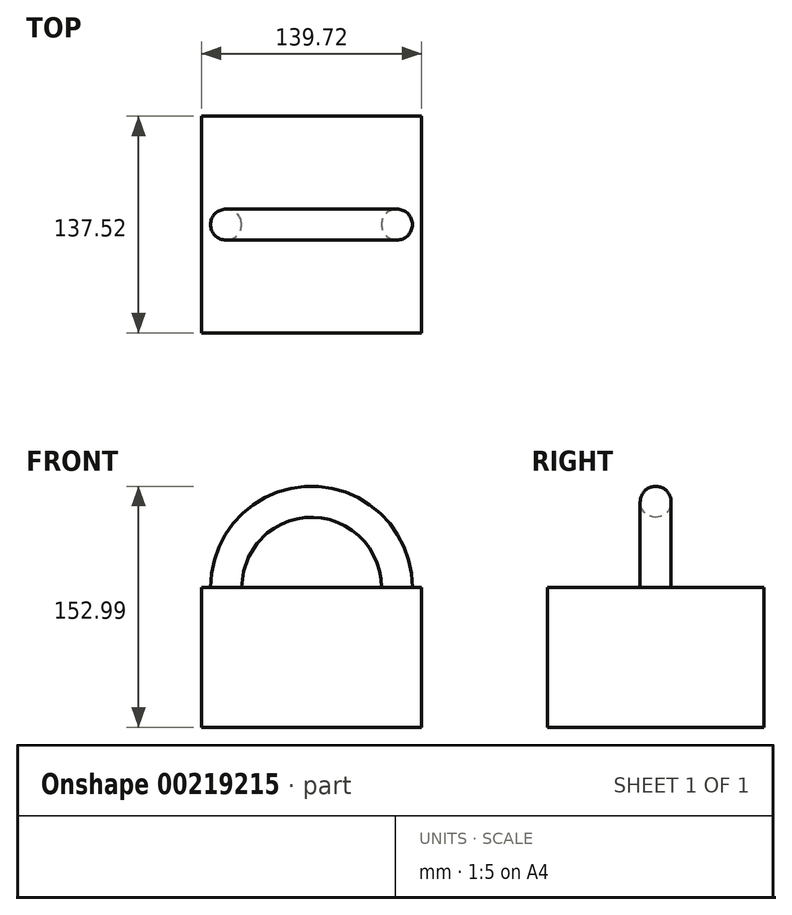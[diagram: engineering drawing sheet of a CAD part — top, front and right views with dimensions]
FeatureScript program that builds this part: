
annotation { "Feature Type Name" : "Feature", "Feature Type Description" : "" }
export const myFeature = defineFeature(function(context is Context, id is Id, definition is map)
    precondition{}
    {
        {
            var Q0;
            Q0=qCreatedBy(makeId("Top.planeOp"),FACE);
            var sketch = newSketch(context, id + "F0", { "sketchPlane" : qUnion([Q0])});
            skLineSegment(sketch, "E0.bottom", {"start": v(69.86, -68.76) * mm, "end": v(-69.86, -68.76) * mm});
            skLineSegment(sketch, "E0.top", {"start": v(69.86, 68.76) * mm, "end": v(-69.86, 68.76) * mm});
            skLineSegment(sketch, "E0.left", {"start": v(69.86, -68.76) * mm, "end": v(69.86, 68.76) * mm});
            skLineSegment(sketch, "E0.right", {"start": v(-69.86, -68.76) * mm, "end": v(-69.86, 68.76) * mm});
            skPoint(sketch, "E0.middle", {"position": v(0, 0) * mm});
            skLineSegment(sketch, "E1", {"start": v(0, 68.76) * mm, "end": v(0, -68.76) * mm});
            skSolve(sketch);
        }
        {
            var Q0;
            Q0=qCreatedBy(makeId("Top.planeOp"),FACE);
            var sketch = newSketch(context, id + "F1", { "sketchPlane" : qUnion([Q0])});
            skCircle(sketch, "E2", {"center": v(54.26, 0) * mm, "radius": 9.82 * mm});
            skSolve(sketch);
        }
        {
            var Q0;
            {var subQ0=sQuery(id+"F0.wireOp",EDGE,"E0.right");Q0=makeQuery(id+"F0.imprint","IMPRINT",FACE,{"disambiguationData":[TD([[makeQuery(id+"F0.imprint","IMPRINT",EDGE,{"derivedFrom":subQ0}),-1.0]])]});}
            var Q1;
            {var subQ0=sQuery(id+"F0.wireOp",EDGE,"E0.left");Q1=makeQuery(id+"F0.imprint","IMPRINT",FACE,{"disambiguationData":[TD([[makeQuery(id+"F0.imprint","IMPRINT",EDGE,{"derivedFrom":subQ0}),1.0]])]});}
            extrude(context, id + "F2", {"entities" : qUnion([Q0, Q1]), "depth" : 88.9 * mm});
        }
        {
            var Q0;
            Q0=makeQuery(id+"F2.opExtrude","CAP_FACE",FACE,{"disambiguationData":[OSD([sQuery(id+"F0.wireOp",EDGE,"E0.bottom"),sQuery(id+"F0.wireOp",EDGE,"E0.top"),sQuery(id+"F0.wireOp",EDGE,"E0.left"),sQuery(id+"F0.wireOp",EDGE,"E0.right")])],"isStart":false});
            var sketch = newSketch(context, id + "F3", { "sketchPlane" : qUnion([Q0])});
            skCircle(sketch, "E3.0", {"center": v(54.26, 0) * mm, "radius": 9.82 * mm});
            skLineSegment(sketch, "E4.0", {"start": v(0, 68.76) * mm, "end": v(0, -68.76) * mm});
            skSolve(sketch);
        }
        {
            var Q0;
            Q0=makeQuery(id+"F3.imprint","IMPRINT",FACE,{"disambiguationData":[TD([[makeQuery(id+"F3.imprint","IMPRINT",EDGE,{"derivedFrom":sQuery(id+"F3.wireOp",EDGE,"E3.0")}),1.0]])]});
            var Q1;
            Q1=sQuery(id+"F3.wireOp",EDGE,"E4.0");
            revolve(context, id + "F4", {"operationType" : NewBodyOperationType.ADD, "entities" : qUnion([Q0]), "axis" : qUnion([Q1]), "revolveType" : RevolveType.FULL});
        }
    });
